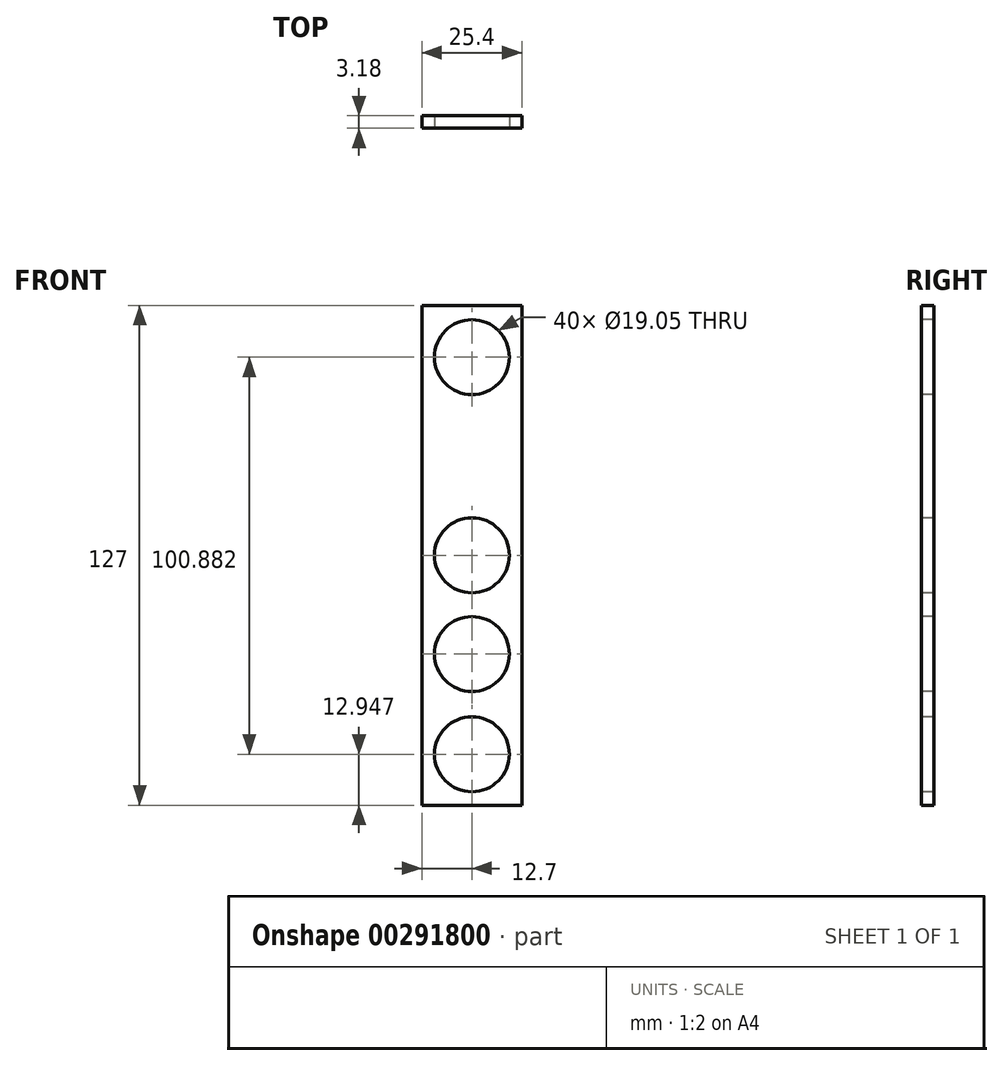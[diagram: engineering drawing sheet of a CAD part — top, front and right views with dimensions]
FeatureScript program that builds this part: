
annotation { "Feature Type Name" : "Feature", "Feature Type Description" : "" }
export const myFeature = defineFeature(function(context is Context, id is Id, definition is map)
    precondition{}
    {
        {
            var Q0;
            Q0=qCreatedBy(makeId("Front.planeOp"),FACE);
            var sketch = newSketch(context, id + "F0", { "sketchPlane" : qUnion([Q0])});
            skLineSegment(sketch, "E0.bottom", {"start": v(12.7, 63.5) * mm, "end": v(-12.7, 63.5) * mm});
            skLineSegment(sketch, "E0.top", {"start": v(12.7, -63.5) * mm, "end": v(-12.7, -63.5) * mm});
            skLineSegment(sketch, "E0.left", {"start": v(12.7, 63.5) * mm, "end": v(12.7, -63.5) * mm});
            skLineSegment(sketch, "E0.right", {"start": v(-12.7, 63.5) * mm, "end": v(-12.7, -63.5) * mm});
            skPoint(sketch, "E0.middle", {"position": v(0, 0) * mm});
            skSolve(sketch);
        }
        {
            var Q0;
            Q0 = qSketchRegion(id + "F0", true);
            extrude(context, id + "F1", {"entities" : qUnion([Q0]), "endBound" : BoundingType.SYMMETRIC, "depth" : 3.17 * mm});
        }
        {
            var Q0;
            Q0=makeQuery(id+"F1.opExtrude","CAP_FACE",FACE,{"disambiguationData":[OSD([sQuery(id+"F0.wireOp",EDGE,"E0.bottom"),sQuery(id+"F0.wireOp",EDGE,"E0.top"),sQuery(id+"F0.wireOp",EDGE,"E0.left"),sQuery(id+"F0.wireOp",EDGE,"E0.right")])],"isStart":false});
            var sketch = newSketch(context, id + "F2", { "sketchPlane" : qUnion([Q0])});
            skCircle(sketch, "E1", {"center": v(0, 50.33) * mm, "radius": 9.53 * mm});
            skSolve(sketch);
        }
        {
            var Q0;
            Q0 = qSketchRegion(id + "F2", true);
            extrude(context, id + "F3", {"entities" : qUnion([Q0]), "operationType" : NewBodyOperationType.REMOVE, "oppositeDirection" : true, "depth" : 25.4 * mm});
        }
        {
            var Q0;
            Q0=makeQuery(id+"F1.opExtrude","CAP_FACE",FACE,{"disambiguationData":[OSD([sQuery(id+"F0.wireOp",EDGE,"E0.bottom"),sQuery(id+"F0.wireOp",EDGE,"E0.top"),sQuery(id+"F0.wireOp",EDGE,"E0.left"),sQuery(id+"F0.wireOp",EDGE,"E0.right")])],"isStart":false});
            var sketch = newSketch(context, id + "F4", { "sketchPlane" : qUnion([Q0])});
            skCircle(sketch, "E2", {"center": v(0, -50.55) * mm, "radius": 9.53 * mm});
            skSolve(sketch);
        }
        {
            var Q0;
            Q0 = qSketchRegion(id + "F4", true);
            extrude(context, id + "F5", {"entities" : qUnion([Q0]), "operationType" : NewBodyOperationType.REMOVE, "oppositeDirection" : true, "depth" : 25.4 * mm});
        }
        {
            var Q0;
            Q0=makeQuery(id+"F1.opExtrude","CAP_FACE",FACE,{"disambiguationData":[OSD([sQuery(id+"F0.wireOp",EDGE,"E0.bottom"),sQuery(id+"F0.wireOp",EDGE,"E0.top"),sQuery(id+"F0.wireOp",EDGE,"E0.left"),sQuery(id+"F0.wireOp",EDGE,"E0.right")])],"isStart":false});
            var sketch = newSketch(context, id + "F6", { "sketchPlane" : qUnion([Q0])});
            skCircle(sketch, "E3", {"center": v(0, 0) * mm, "radius": 9.53 * mm});
            skSolve(sketch);
        }
        {
            var Q0;
            Q0 = qSketchRegion(id + "F6", true);
            extrude(context, id + "F7", {"entities" : qUnion([Q0]), "operationType" : NewBodyOperationType.REMOVE, "oppositeDirection" : true, "depth" : 25.4 * mm});
        }
        {
            var Q0;
            Q0=makeQuery(id+"F1.opExtrude","CAP_FACE",FACE,{"disambiguationData":[OSD([sQuery(id+"F0.wireOp",EDGE,"E0.bottom"),sQuery(id+"F0.wireOp",EDGE,"E0.top"),sQuery(id+"F0.wireOp",EDGE,"E0.left"),sQuery(id+"F0.wireOp",EDGE,"E0.right")])],"isStart":false});
            var sketch = newSketch(context, id + "F8", { "sketchPlane" : qUnion([Q0])});
            skCircle(sketch, "E4", {"center": v(0, -25.1) * mm, "radius": 9.53 * mm});
            skSolve(sketch);
        }
        {
            var Q0;
            Q0 = qSketchRegion(id + "F8", true);
            extrude(context, id + "F9", {"entities" : qUnion([Q0]), "operationType" : NewBodyOperationType.REMOVE, "oppositeDirection" : true, "depth" : 25.4 * mm});
        }
    });
